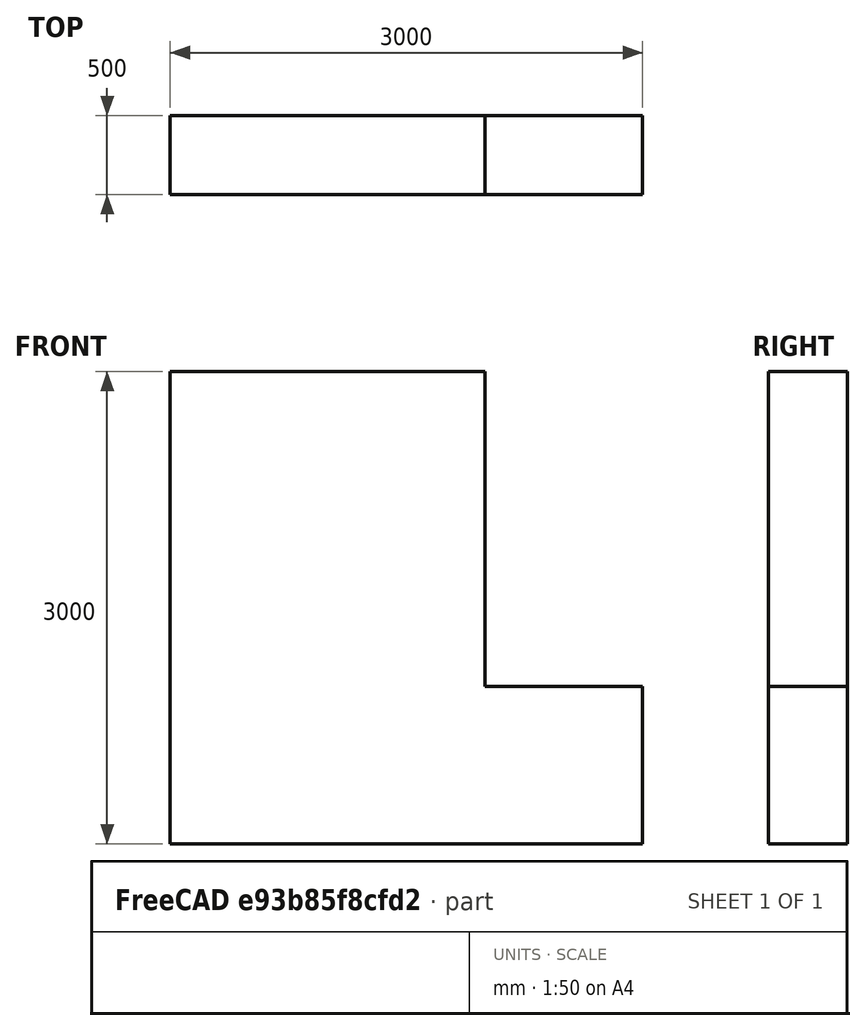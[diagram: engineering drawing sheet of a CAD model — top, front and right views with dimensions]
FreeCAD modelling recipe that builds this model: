
FCSTD DOCUMENT  (FreeCAD 0.21R33694 (Git))
Label: Trench_Example
License: All rights reserved
LicenseURL: http://en.wikipedia.org/wiki/All_rights_reserved
objects: Fem::FemMeshObjectPython×2, Sketcher::SketchObject×1, PartDesign::Pad×1, PartDesign::Body×1, Fem::FemSolverObjectPython×1, App::MaterialObjectPython×1, Fem::ConstraintFixed×1, Fem::ConstraintDisplacement×1, Fem::FemResultObjectPython×1, Fem::FemAnalysis×1
note: 4 computed .brp shape members not serialized (recipe doc carries the construction recipe); baked Part::Feature solids carry a one-line shape summary decoded from their .brp

FEATURE [Sketcher::SketchObject] Sketch
  FullyConstrained = true
  MapMode = 5
  Placement = pos=(0,0,0) rot=(1,0,0;1.5708rad)
  Support = -> [XZ_Plane]
  sketch-geometry (6):
    g0: LineSegment StartX=0 StartY=0 StartZ=0 EndX=3000 EndY=0 EndZ=0
    g1: LineSegment StartX=0 StartY=0 StartZ=0 EndX=0 EndY=3000 EndZ=0
    g2: LineSegment StartX=0 StartY=3000 StartZ=0 EndX=2000 EndY=3000 EndZ=0
    g3: LineSegment StartX=2000 StartY=3000 StartZ=0 EndX=2000 EndY=1000 EndZ=0
    g4: LineSegment StartX=2000 StartY=1000 StartZ=0 EndX=3000 EndY=1000 EndZ=0
    g5: LineSegment StartX=3000 StartY=1000 StartZ=0 EndX=3000 EndY=0 EndZ=0
  constraints (18):
    c: Coincident(g0,g-1)
    c: Horizontal(g0)
    c: Distance(g0) = 3000
    c: Coincident(g1,g0)
    c: PointOnObject(g1,g-2)
    c: Coincident(g2,g1)
    c: Horizontal(g2)
    c: Coincident(g3,g2)
    c: Vertical(g3)
    c: Horizontal(g4)
    c: Coincident(g5,g0)
    c: Distance(g2) = 2000
    c: Distance(g4) = 1000
    c: Distance(g5) = 1000
    c: Distance(g1) = 3000
    c: Distance(g3) = 2000
    c: Coincident(g3,g4)
    c: Vertical(g5)
FEATURE [PartDesign::Pad] Pad
  Direction = (0,-1,-2e-16)
  Length = 500
  Length2 = 10
  Placement = pos=(0,0,0) rot=(1,0,0;1.5708rad)
  Profile = -> Sketch
  ReferenceAxis = -> Sketch [N_Axis]
  Type = 0
FEATURE [PartDesign::Body] Body
  Group = -> [Sketch,Pad]
  Origin = -> Origin
  Tip = -> Pad
FEATURE [Fem::FemSolverObjectPython] SolverCcxTools  # FEM object (typed FeaturePython)
  AnalysisType = 0
  BeamShellResultOutput3D = false
  BucklingFactors = 1
  EigenmodeHighLimit = 1000000
  EigenmodeLowLimit = 0
  EigenmodesCount = 10
  GeometricalNonlinearity = 0
  IterationsControlParameterCutb = 0.25,0.5,0.75,0.85,,,1.5,
  IterationsControlParameterIter = 4,8,9,200,10,400,,200,,
  IterationsControlParameterTimeUse = false
  IterationsThermoMechMaximum = 2000
  IterationsUserDefinedIncrementations = false
  IterationsUserDefinedTimeStepLength = false
  MaterialNonlinearity = 0
  MatrixSolverType = 0
  SplitInputWriter = false
  ThermoMechSteadyState = true
  TimeEnd = 1
  TimeInitialStep = 0.01
FEATURE [Fem::FemMeshObjectPython] FEMMeshGmsh  # FEM object (typed FeaturePython)
  Algorithm2D = 0
  Algorithm3D = 0
  CharacteristicLengthMax = 0
  CharacteristicLengthMin = 0
  CoherenceMesh = true
  ElementDimension = 0
  ElementOrder = 1
  GeometryTolerance = 1e-06
  GroupsOfNodes = false
  HighOrderOptimize = 0
  MeshSizeFromCurvature = 12
  OptimizeNetgen = false
  OptimizeStd = true
  Part = -> Body
  RecombinationAlgorithm = 0
  Recombine3DAll = false
  RecombineAll = false
  SecondOrderLinear = false
FEATURE [App::MaterialObjectPython] MaterialSolid  # material (typed FeaturePython)
  Category = 0
  Material = Density=2000.0000000000002 kg/m^3; Name=NoName; PoissonRatio=0.45; YoungsModulus=5000.0 kPa
  References = -> [Pad]
FEATURE [Fem::ConstraintFixed] ConstraintFixed
  NormalDirection = (-1,0,0)
  Normals = (80) [(-1,0,0),(-1,0,0),(-1,0,0),(-1,0,0),(-1,0,0),(-1,0,0),(-1,0,0),(-1,0,0),(-1,0,0),(-1,0,0),(-1,0,0),(-1,0,0),(-1,0,0),(-1,0,0),(-1,0,0),(-1,0,0),+64 more]
  Points = (80) [(0,-500,0),(0,-500,428.571),(0,-500,857.143),(0,-500,1285.71),(0,-500,1714.29),(0,-500,2142.86),(0,-500,2571.43),(0,-500,3000),(0,-333.333,0),+71 more]
  References = -> [Pad]
  Scale = 29
FEATURE [Fem::ConstraintDisplacement] ConstraintDisplacement
  NormalDirection = (0,-1,-2e-16)
  Normals = (82) [(0,-1,-2.2e-16),(0,-1,-2.2e-16),(0,-1,-2.2e-16),(0,-1,-2.2e-16),(0,-1,-2.2e-16),(0,-1,-2.2e-16),(0,-1,-2.2e-16),(0,-1,-2.2e-16),(0,-1,-2.2e-16),+73 more]
  Points = (82) [(0,-500,0),(0,-500,500),(0,-500,1000),(0,-500,1500),(0,-500,2000),(0,-500,2500),(0,-500,3000),(500,-500,0),(500,-500,500),(500,-500,1000),+72 more]
  References = -> [Pad]
  Scale = 51
  hasXFormula = false
  hasYFormula = false
  hasZFormula = false
  rotxFix = false
  rotxFree = true
  rotyFix = false
  rotyFree = true
  rotzFix = false
  rotzFree = true
  useFlowSurfaceForce = false
  xDisplacement = 0
  xFix = false
  xFree = true
  xRotation = 0
  yDisplacement = 0
  yFix = true
  yFree = false
  yRotation = 0
  zDisplacement = 0
  zFix = false
  zFree = true
  zRotation = 0
FEATURE [Fem::FemMeshObjectPython] Result_Mesh_Volume  # FEM object (typed FeaturePython)
FEATURE [Fem::FemResultObjectPython] ResultMechanical  # FEM object (typed FeaturePython)
  DisplacementLengths = [0,0,0,0,0,0,0.29114,0.324325,0.807025,0.807077,0,0,0,0,0,0,0,0,0,0,0,0,0,0,0,0,0,0,0,0,0,0,0,0,0,0,0,0,0,0,0,0,0,0,0,0,0,0,0,0,0,0,0,0,0,0,0,0,0,0,0,0.189769,0.252636,0.250512,0.0311027,0.00717205,0.171745,0.0142312,0.00374198,0.0324342,+1054 more]
  DisplacementVectors = (1124) [(0,0,0),(0,0,0),(0,0,0),(0,0,0),(0,0,0),(0,0,0),(0.289183,0,-0.0337025),(0.321341,0,-0.043889),(0.420867,0,-0.688593),(0.420906,0,-0.68863),(0,0,0),+1113 more]
  Eigenmode = 0
  EigenmodeFrequency = 0
  MaxShear = [0.00222352,0.00222279,0.00161401,0.00161788,0.0073971,0.00739695,0.00994222,0.0107157,0.000176462,0.000170684,0.0111679,0.0111474,3.57906e-18,2.60385e-18,3.72691e-18,1.33016e-17,1.77133e-17,1.33541e-17,0.0058254,0.00511678,0.00554207,+1103 more]
  Mesh = -> Result_Mesh_Volume
  NodeNumbers = [1,2,3,4,5,6,7,8,9,10,11,12,13,14,15,16,17,18,19,20,21,22,23,24,25,26,27,28,29,30,31,32,33,34,35,36,37,38,39,40,41,42,43,44,45,46,47,48,49,50,51,52,53,54,55,56,57,58,59,60,61,62,63,64,65,66,67,68,69,+1055 more]
  NodeStressXX = [-0.0217684,-0.0217599,-0.0153224,-0.0154265,-0.021024,-0.0210591,-0.024482,-0.0250955,-0.000258999,-0.000250071,0.0645622,0.0645138,-1.19821e-17,-5.63606e-18,-1.18448e-17,-5.11919e-17,-1.41398e-16,1.71712e-18,-0.0378593,-0.0426427,+1104 more]
  NodeStressXY = [-0.00038714,0.0003865,0.00023047,-0.00022039,0.000114268,-0.000110523,0.000633896,-0.00177278,-7.37217e-06,5.98462e-06,-0.000298162,0.000319434,-2.75738e-21,-4.87027e-20,3.45887e-21,8.22179e-18,8.12737e-18,8.30222e-18,-1.6568e-05,+1105 more]
  NodeStressXZ = [-0.00215664,-0.00215619,0.0015536,0.00155865,-0.00626319,-0.00626363,0.00942631,0.0100913,0.00016913,0.00016455,-0.00994263,-0.00990576,-5.89246e-19,-2.85401e-19,-5.99954e-19,4.74727e-18,1.50472e-17,-1.21584e-18,-0.00408024,-0.00193184,+1104 more]
  NodeStressYY = [-0.0194379,-0.0194333,-0.0139828,-0.0140977,-0.0152349,-0.0152815,-0.0267362,-0.0258179,-0.000282569,-0.000259268,0.061378,0.06133,-1.27396e-17,-1.08027e-17,-1.00364e-17,-3.96882e-17,-1.26424e-16,1.14861e-17,-0.0378152,-0.0426427,+1104 more]
  NodeStressYZ = [-0.000337471,0.00033795,-0.000304054,0.000288274,-0.000297772,0.000340167,-0.0005621,0.000840689,2.57665e-05,-2.40742e-05,-0.000340427,0.000341225,-3.09534e-21,-5.67584e-20,3.83698e-21,-7.44792e-18,-7.36319e-18,-7.52047e-18,2.25371e-05,+1105 more]
  NodeStressZZ = [-0.0214269,-0.0214251,-0.0157504,-0.0159018,-0.013187,-0.0132325,-0.0305895,-0.0312427,-0.000178433,-0.0001766,0.0544253,0.0543254,-5.63571e-18,-7.67753e-18,-4.48822e-18,-4.1197e-17,-1.36275e-16,1.57176e-17,-0.0461744,-0.0521189,-0.055638,+1103 more]
  Peeq = [0,0,0,0,0,0,0.0404772,0.0405961,0,0,0.0214765,0.0214573,0,0,0,0,0,0,0,0,0,0,0,0,0,0,0,0,0,0,0,0,0,0,0,0,0,0,0,0,0,0,0,0,0,0,0,0,0,0,0,0,0,0,0,0,0,0,0,0,0,0.0227111,0.0364761,0.0369779,0.000673434,0,0.0122206,0,0,0.000825407,0,0.0137196,0,0,+1050 more]
  PrincipalMax = [-0.0193742,-0.0193697,-0.0139224,-0.0140463,-0.00969954,-0.00973797,-0.0176235,-0.0175155,-4.38232e-05,-4.36794e-05,0.0706544,0.0705594,-5.58146e-18,-5.59659e-18,-4.43961e-18,-3.23324e-17,-1.22489e-16,2.32452e-17,-0.0361913,-0.042264,+1104 more]
  PrincipalMed = [-0.0194379,-0.0194333,-0.0139828,-0.0140977,-0.0152527,-0.0153033,-0.0266762,-0.0256937,-0.00027943,-0.000257214,0.0613926,0.061345,-1.20363e-17,-7.7154e-18,-1.00364e-17,-4.08093e-17,-1.23694e-16,9.13856e-18,-0.0378155,-0.0426427,+1104 more]
  PrincipalMin = [-0.0238212,-0.0238153,-0.0171504,-0.017282,-0.0244937,-0.0245319,-0.0375079,-0.0389469,-0.000396748,-0.000385047,0.0483186,0.0482646,-1.27396e-17,-1.08043e-17,-1.18934e-17,-5.89355e-17,-1.57915e-16,-3.46298e-18,-0.0478421,-0.0524976,+1104 more]
  ResultType = Fem::ResultMechanical
  Stats = [0,0,0,0,0,0,0,0,0,0,0,0,0,0,0,0,0,0,0,0,0,0,0,0,0,0]
  Time = 0
  vonMises = [0.0044155,0.00441415,0.00319827,0.00321033,0.0129442,0.0129422,0.0172434,0.0187328,0.000311311,0.000298722,0.0194371,0.0194044,6.83367e-18,4.536e-18,6.72058e-18,2.35388e-17,3.48397e-17,2.31422e-17,0.0109296,0.0100496,0.0108369,0.0142725,+1102 more]
FEATURE [Fem::FemAnalysis] Analysis
  Group = -> [SolverCcxTools,FEMMeshGmsh,MaterialSolid,ConstraintFixed,ConstraintDisplacement,ResultMechanical]
